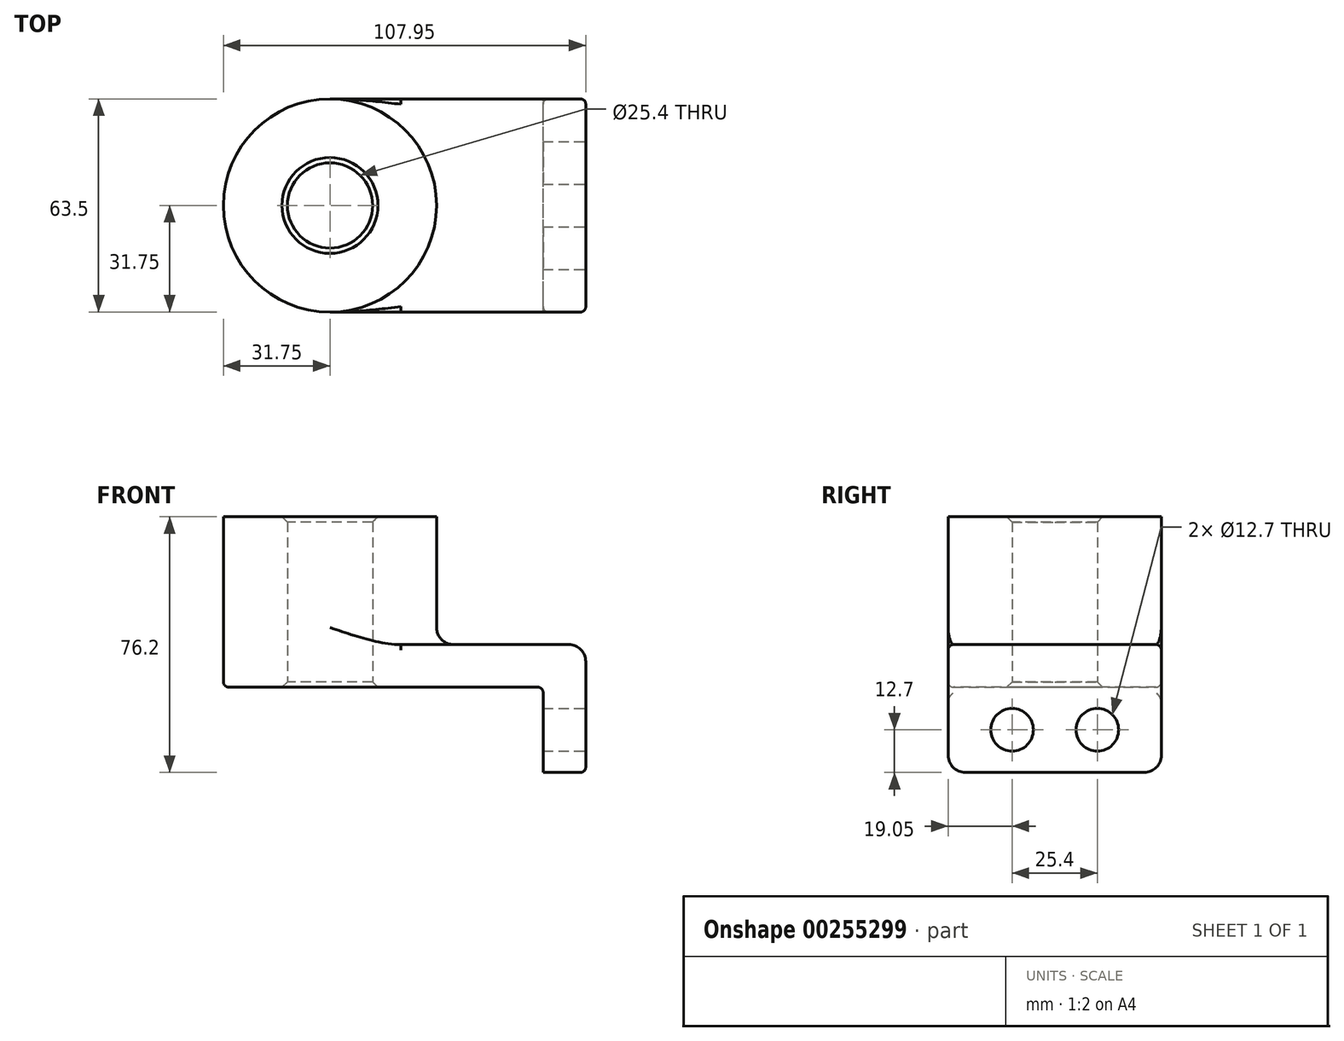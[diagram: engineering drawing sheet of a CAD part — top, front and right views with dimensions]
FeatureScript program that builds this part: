
annotation { "Feature Type Name" : "Feature", "Feature Type Description" : "" }
export const myFeature = defineFeature(function(context is Context, id is Id, definition is map)
    precondition{}
    {
        {
            var Q0;
            Q0=qCreatedBy(makeId("Top.planeOp"),FACE);
            var sketch = newSketch(context, id + "F0", { "sketchPlane" : qUnion([Q0])});
            skLineSegment(sketch, "E0.bottom", {"start": v(38.1, -31.75) * mm, "end": v(-38.1, -31.75) * mm});
            skLineSegment(sketch, "E0.top", {"start": v(38.1, 31.75) * mm, "end": v(-38.1, 31.75) * mm});
            skLineSegment(sketch, "E0.left", {"start": v(38.1, -31.75) * mm, "end": v(38.1, 31.75) * mm});
            skLineSegment(sketch, "E0.right", {"start": v(-38.1, -31.75) * mm, "end": v(-38.1, 31.75) * mm});
            skPoint(sketch, "E0.middle", {"position": v(0, 0) * mm});
            skCircle(sketch, "E1", {"center": v(-38.1, 0) * mm, "radius": 31.75 * mm});
            skCircle(sketch, "E2", {"center": v(-38.1, 0) * mm, "radius": 12.7 * mm});
            skSolve(sketch);
        }
        {
            var Q0;
            Q0=qSketchRegion(id+"F0",true);
            extrude(context, id + "F1", {"entities" : qUnion([Q0]), "depth" : 12.7 * mm});
        }
        {
            var Q0;
            {var subQ1=sQuery(id+"F0.wireOp",EDGE,"E0.right");var subQ3=sQuery(id+"F0.wireOp",EDGE,"E2");var subQ4=makeQuery(id+"F0.imprint","INTERSECT",VERTEX,{"disambiguationData":[OD(0.0)],"derivedFrom":[subQ1,subQ3]});Q0=makeQuery(id+"F0.imprint","IMPRINT",FACE,{"disambiguationData":[TD([[makeQuery(id+"F0.imprint","IMPRINT",EDGE,{"disambiguationData":[TD([[subQ4,1.0]])],"derivedFrom":subQ3}),-1.0]])]});}
            var Q1;
            {var subQ1=sQuery(id+"F0.wireOp",EDGE,"E0.right");var subQ3=sQuery(id+"F0.wireOp",EDGE,"E2");var subQ4=makeQuery(id+"F0.imprint","INTERSECT",VERTEX,{"disambiguationData":[OD(0.0)],"derivedFrom":[subQ1,subQ3]});Q1=makeQuery(id+"F0.imprint","IMPRINT",FACE,{"disambiguationData":[TD([[makeQuery(id+"F0.imprint","IMPRINT",EDGE,{"disambiguationData":[TD([[subQ4,-1.0]])],"derivedFrom":subQ3}),-1.0]])]});}
            extrude(context, id + "F2", {"entities" : qUnion([Q0, Q1]), "operationType" : NewBodyOperationType.ADD, "depth" : 50.8 * mm});
        }
        {
            var Q0;
            Q0=makeQuery(id+"F1.opExtrude","SWEPT_FACE",FACE,{"disambiguationData":[OSD([sQuery(id+"F0.wireOp",EDGE,"E0.left")])]});
            var sketch = newSketch(context, id + "F3", { "sketchPlane" : qUnion([Q0])});
            skLineSegment(sketch, "E3.bottom", {"start": v(-31.75, 12.7) * mm, "end": v(31.75, 12.7) * mm});
            skLineSegment(sketch, "E3.top", {"start": v(-31.75, -25.4) * mm, "end": v(31.75, -25.4) * mm});
            skLineSegment(sketch, "E3.left", {"start": v(-31.75, 12.7) * mm, "end": v(-31.75, -25.4) * mm});
            skLineSegment(sketch, "E3.right", {"start": v(31.75, 12.7) * mm, "end": v(31.75, -25.4) * mm});
            skCircle(sketch, "E4", {"center": v(-12.7, -12.7) * mm, "radius": 6.35 * mm});
            skLineSegment(sketch, "E5", {"start": v(0, 0) * mm, "end": v(0, -25.4) * mm});
            skCircle(sketch, "E6.MirrorC", {"center": v(12.7, -12.7) * mm, "radius": 6.35 * mm});
            skSolve(sketch);
        }
        {
            var Q0;
            Q0=qSketchRegion(id+"F3",true);
            extrude(context, id + "F4", {"entities" : qUnion([Q0]), "operationType" : NewBodyOperationType.ADD, "oppositeDirection" : true, "depth" : 12.7 * mm});
        }
        {
            var Q0;
            {var subQ0=sQuery(id+"F0.wireOp",EDGE,"E1");Q0=makeQuery(id+"F2.boolean.opBoolean","INTERSECT",EDGE,{"derivedFrom":[makeQuery(id+"F1.opExtrude","CAP_FACE",FACE,{"disambiguationData":[OSD([sQuery(id+"F0.wireOp",EDGE,"E0.bottom"),sQuery(id+"F0.wireOp",EDGE,"E0.top"),sQuery(id+"F0.wireOp",EDGE,"E0.left"),subQ0,sQuery(id+"F0.wireOp",EDGE,"E2")])],"isStart":false}),makeQuery(id+"F2.opExtrude","SWEPT_FACE",FACE,{"disambiguationData":[OSD([subQ0])]})]});}
            var Q1;
            Q1=makeQuery(id+"F1.opExtrude","CAP_EDGE",EDGE,{"disambiguationData":[OSD([sQuery(id+"F0.wireOp",EDGE,"E0.left")])],"isStart":false});
            var Q2;
            Q2=makeQuery(id+"F4.opExtrude","SWEPT_EDGE",EDGE,{"disambiguationData":[OSD([sQuery(id+"F3.wireOp",EDGE,"E3.top"),sQuery(id+"F3.wireOp",EDGE,"E3.left")])]});
            var Q3;
            Q3=makeQuery(id+"F4.opExtrude","SWEPT_EDGE",EDGE,{"disambiguationData":[OSD([sQuery(id+"F3.wireOp",EDGE,"E3.top"),sQuery(id+"F3.wireOp",EDGE,"E3.right")])]});
            fillet(context, id + "F5", {"entities" : qUnion([Q0, Q1, Q2, Q3]), "radius" : 5.08 * mm, "tangentPropagation" : true, "allowEdgeOverflow" : false});
        }
        {
            var Q0;
            Q0=makeQuery(id+"F1.opExtrude","CAP_EDGE",EDGE,{"disambiguationData":[OSD([sQuery(id+"F0.wireOp",EDGE,"E0.bottom")])],"isStart":false});
            var Q1;
            Q1=makeQuery(id+"F1.opExtrude","CAP_EDGE",EDGE,{"disambiguationData":[OSD([sQuery(id+"F0.wireOp",EDGE,"E0.bottom")])],"isStart":true});
            var Q2;
            Q2=makeQuery(id+"F4.boolean.opBoolean","INTERSECT",EDGE,{"derivedFrom":[makeQuery(id+"F1.opExtrude","CAP_FACE",FACE,{"disambiguationData":[OSD([sQuery(id+"F0.wireOp",EDGE,"E0.bottom"),sQuery(id+"F0.wireOp",EDGE,"E0.top"),sQuery(id+"F0.wireOp",EDGE,"E0.left"),sQuery(id+"F0.wireOp",EDGE,"E1"),sQuery(id+"F0.wireOp",EDGE,"E2")])],"isStart":true}),makeQuery(id+"F4.opExtrude","CAP_FACE",FACE,{"disambiguationData":[OSD([sQuery(id+"F3.wireOp",EDGE,"E3.bottom"),sQuery(id+"F3.wireOp",EDGE,"E3.top"),sQuery(id+"F3.wireOp",EDGE,"E3.left"),sQuery(id+"F3.wireOp",EDGE,"E3.right"),sQuery(id+"F3.wireOp",EDGE,"E4"),sQuery(id+"F3.wireOp",EDGE,"E6.MirrorC")])],"isStart":false})]});
            fillet(context, id + "F6", {"entities" : qUnion([Q0, Q1, Q2]), "radius" : 1.59 * mm, "tangentPropagation" : true, "allowEdgeOverflow" : false});
        }
        {
            var Q0;
            {var subQ0=sQuery(id+"F0.wireOp",EDGE,"E2");Q0=makeQuery(id+"F2.boolean.opBoolean","MERGE",FACE,{"derivedFrom":[makeQuery(id+"F1.opExtrude","SWEPT_FACE",FACE,{"disambiguationData":[OSD([subQ0])]}),makeQuery(id+"F2.opExtrude","SWEPT_FACE",FACE,{"disambiguationData":[OSD([subQ0])]})]});}
            chamfer(context, id + "F7", {"entities" : qUnion([Q0]), "width" : 1.59 * mm, "tangentPropagation" : true});
        }
    });
